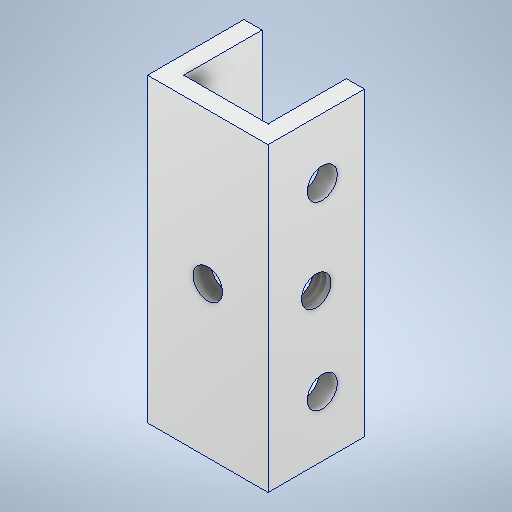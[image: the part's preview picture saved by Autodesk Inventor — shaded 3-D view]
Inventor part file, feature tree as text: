
AUTODESK INVENTOR PART (.ipt)
format: ipt  version: 2025 (Build 290162000, 162)  size: 280,576 bytes
history: native  units: mm
features: sketch x4, hole x3, other x1, extrude x1, projected_geometry x1
ambient origin geometry x8: Origin, YZ Plane, XZ Plane, XY Plane, X Axis, Y Axis, Z Axis, Center Point
bodies: Body1 (feature_tree)
feature tree (10):
  other  "Těleso1"
  extrude  "Vysunutí1"  Depth=8.0mm
  hole  "Díra1"  [1 undecoded]
  hole  "Díra2"  [1 undecoded]
  hole  "Díra3"  [1 undecoded]
  sketch  "Náčrt1"
  sketch  "Náčrt2"
  sketch  "Náčrt3"
  sketch  "Náčrt4"
  projected_geometry  "Promítnutá smyčka1"
note: 3 required parameter values undecoded (feature->parameter linkage not recoverable at this tier; creation-order binding heuristic only, values carry confidence <= 0.55)
